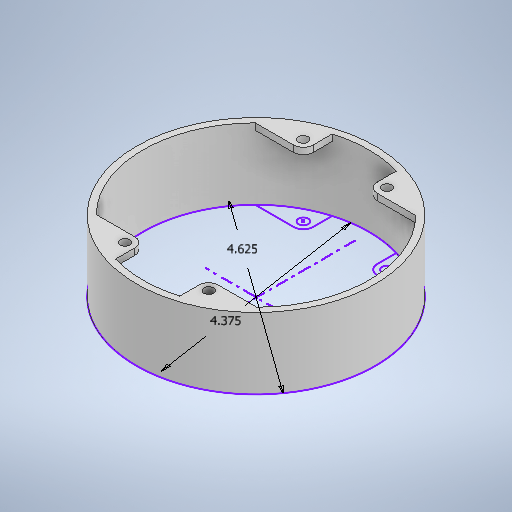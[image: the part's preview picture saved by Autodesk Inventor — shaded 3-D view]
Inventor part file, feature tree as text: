
AUTODESK INVENTOR PART (.ipt)
format: ipt  version: 2025.1 (Build 291241000, 241)  size: 305,152 bytes
history: native  units: in
note: dims shown in document units (in); Inventor stores cm internally (conversion verified against a paired STEP export)
features: extrude x2, sketch x1
ambient origin geometry x8: Origin, YZ Plane, XZ Plane, XY Plane, X Axis, Y Axis, Z Axis, Center Point
bodies: Solid1 (feature_tree)
feature tree (3):
  sketch  "Sketch1"  dims[d3=4.375in d4=4.625in d22=1.375in d23=0.0in d24=1.25in d25=0.0in]
  extrude  "Extrusion1"  Depth=1.25in
  extrude  "Extrusion2"  Depth=1.375in TaperAngle=0.0deg
